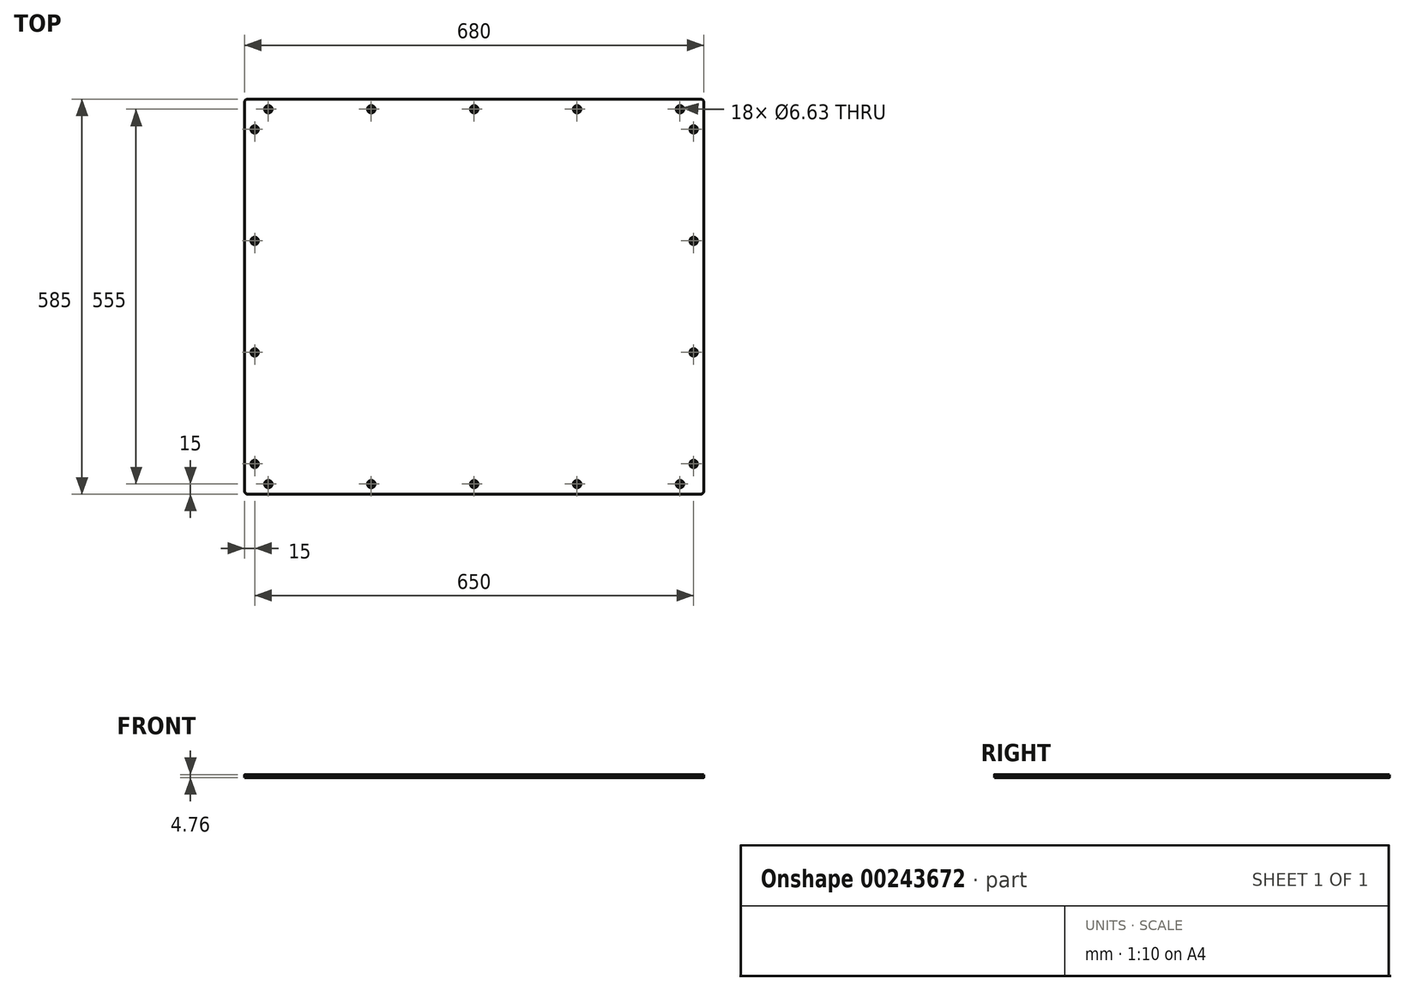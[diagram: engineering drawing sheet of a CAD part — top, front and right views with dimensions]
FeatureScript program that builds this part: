
annotation { "Feature Type Name" : "Feature", "Feature Type Description" : "" }
export const myFeature = defineFeature(function(context is Context, id is Id, definition is map)
    precondition{}
    {
        {
            var Q0;
            Q0=qCreatedBy(makeId("Top.planeOp"),FACE);
            var sketch = newSketch(context, id + "F0", { "sketchPlane" : qUnion([Q0])});
            skLineSegment(sketch, "E0.bottom", {"start": v(-340, -292.5) * mm, "end": v(340, -292.5) * mm});
            skLineSegment(sketch, "E0.top", {"start": v(-340, 292.5) * mm, "end": v(340, 292.5) * mm});
            skLineSegment(sketch, "E0.left", {"start": v(-340, -292.5) * mm, "end": v(-340, 292.5) * mm});
            skLineSegment(sketch, "E0.right", {"start": v(340, -292.5) * mm, "end": v(340, 292.5) * mm});
            skPoint(sketch, "E0.middle", {"position": v(0, 0) * mm});
            skSolve(sketch);
        }
        {
            var Q0;
            Q0 = qSketchRegion(id + "F0", true);
            extrude(context, id + "F1", {"entities" : qUnion([Q0]), "endBound" : BoundingType.SYMMETRIC, "depth" : 4.76 * mm});
        }
        {
            var Q0;
            Q0=makeQuery(id+"F1.opExtrude","SWEPT_EDGE",EDGE,{"disambiguationData":[OSD([sQuery(id+"F0.wireOp",EDGE,"E0.top"),sQuery(id+"F0.wireOp",EDGE,"E0.right")])]});
            var Q1;
            Q1=makeQuery(id+"F1.opExtrude","SWEPT_EDGE",EDGE,{"disambiguationData":[OSD([sQuery(id+"F0.wireOp",EDGE,"E0.bottom"),sQuery(id+"F0.wireOp",EDGE,"E0.right")])]});
            var Q2;
            Q2=makeQuery(id+"F1.opExtrude","SWEPT_EDGE",EDGE,{"disambiguationData":[OSD([sQuery(id+"F0.wireOp",EDGE,"E0.bottom"),sQuery(id+"F0.wireOp",EDGE,"E0.left")])]});
            var Q3;
            Q3=makeQuery(id+"F1.opExtrude","SWEPT_EDGE",EDGE,{"disambiguationData":[OSD([sQuery(id+"F0.wireOp",EDGE,"E0.top"),sQuery(id+"F0.wireOp",EDGE,"E0.left")])]});
            fillet(context, id + "F2", {"entities" : qUnion([Q0, Q1, Q2, Q3]), "radius" : 4.76 * mm, "tangentPropagation" : true, "allowEdgeOverflow" : false});
        }
        {
            var Q0;
            Q0=makeQuery(id+"F1.opExtrude","CAP_FACE",FACE,{"disambiguationData":[OSD([sQuery(id+"F0.wireOp",EDGE,"E0.bottom"),sQuery(id+"F0.wireOp",EDGE,"E0.top"),sQuery(id+"F0.wireOp",EDGE,"E0.left"),sQuery(id+"F0.wireOp",EDGE,"E0.right")])],"isStart":false});
            var sketch = newSketch(context, id + "F3", { "sketchPlane" : qUnion([Q0])});
            skLineSegment(sketch, "E1", {"start": v(-325, 247.65) * mm, "end": v(-325, 165.1) * mm, "construction": true});
            skLineSegment(sketch, "E2", {"start": v(-325, 165.1) * mm, "end": v(-325, 82.55) * mm, "construction": true});
            skLineSegment(sketch, "E3", {"start": v(-325, 82.55) * mm, "end": v(-325, 0) * mm, "construction": true});
            skLineSegment(sketch, "E4", {"start": v(-325, 0) * mm, "end": v(0, 0) * mm, "construction": true});
            skLineSegment(sketch, "E5", {"start": v(-325, 0) * mm, "end": v(-325, -82.55) * mm, "construction": true});
            skLineSegment(sketch, "E6", {"start": v(-325, -82.55) * mm, "end": v(-325, -165.1) * mm, "construction": true});
            skLineSegment(sketch, "E7", {"start": v(-325, -165.1) * mm, "end": v(-325, -247.65) * mm, "construction": true});
            skLineSegment(sketch, "E8", {"start": v(0, 0) * mm, "end": v(0, 277.5) * mm, "construction": true});
            skLineSegment(sketch, "E9", {"start": v(0, 277.5) * mm, "end": v(-76.2, 277.5) * mm, "construction": true});
            skLineSegment(sketch, "E10", {"start": v(-76.2, 277.5) * mm, "end": v(-152.4, 277.5) * mm, "construction": true});
            skLineSegment(sketch, "E11", {"start": v(-152.4, 277.5) * mm, "end": v(-228.6, 277.5) * mm, "construction": true});
            skLineSegment(sketch, "E12", {"start": v(-228.6, 277.5) * mm, "end": v(-304.8, 277.5) * mm, "construction": true});
            skLineSegment(sketch, "E13", {"start": v(0, 277.5) * mm, "end": v(76.2, 277.5) * mm, "construction": true});
            skLineSegment(sketch, "E14", {"start": v(76.2, 277.5) * mm, "end": v(152.4, 277.5) * mm, "construction": true});
            skLineSegment(sketch, "E15", {"start": v(152.4, 277.5) * mm, "end": v(228.6, 277.5) * mm, "construction": true});
            skLineSegment(sketch, "E16", {"start": v(228.6, 277.5) * mm, "end": v(304.8, 277.5) * mm, "construction": true});
            skLineSegment(sketch, "E17.MirrorCS", {"start": v(228.6, -277.5) * mm, "end": v(304.8, -277.5) * mm, "construction": true});
            skLineSegment(sketch, "E18.MirrorCS", {"start": v(152.4, -277.5) * mm, "end": v(228.6, -277.5) * mm, "construction": true});
            skLineSegment(sketch, "E19.MirrorCS", {"start": v(76.2, -277.5) * mm, "end": v(152.4, -277.5) * mm, "construction": true});
            skLineSegment(sketch, "E20.MirrorCS", {"start": v(0, -277.5) * mm, "end": v(76.2, -277.5) * mm, "construction": true});
            skLineSegment(sketch, "E21.MirrorCS", {"start": v(-228.6, -277.5) * mm, "end": v(-304.8, -277.5) * mm, "construction": true});
            skLineSegment(sketch, "E22.MirrorCS", {"start": v(-152.4, -277.5) * mm, "end": v(-228.6, -277.5) * mm, "construction": true});
            skLineSegment(sketch, "E23.MirrorCS", {"start": v(-76.2, -277.5) * mm, "end": v(-152.4, -277.5) * mm, "construction": true});
            skLineSegment(sketch, "E24.MirrorCS", {"start": v(0, -277.5) * mm, "end": v(-76.2, -277.5) * mm, "construction": true});
            skLineSegment(sketch, "E25.MirrorCS", {"start": v(325, 247.65) * mm, "end": v(325, 165.1) * mm, "construction": true});
            skLineSegment(sketch, "E26.MirrorCS", {"start": v(325, 165.1) * mm, "end": v(325, 82.55) * mm, "construction": true});
            skLineSegment(sketch, "E27.MirrorCS", {"start": v(325, 82.55) * mm, "end": v(325, 0) * mm, "construction": true});
            skLineSegment(sketch, "E28.MirrorCS", {"start": v(325, -82.55) * mm, "end": v(325, -165.1) * mm, "construction": true});
            skLineSegment(sketch, "E29.MirrorCS", {"start": v(325, 0) * mm, "end": v(325, -82.55) * mm, "construction": true});
            skLineSegment(sketch, "E30.MirrorCS", {"start": v(325, -165.1) * mm, "end": v(325, -247.65) * mm, "construction": true});
            skSolve(sketch);
        }
        {
            var Q0;
            Q0=sQuery(id+"F3.wireOp",VERTEX,"E3.start");
            var Q1;
            Q1=sQuery(id+"F3.wireOp",VERTEX,"E1.start");
            var Q2;
            Q2=sQuery(id+"F3.wireOp",VERTEX,"E6.start");
            var Q3;
            Q3=sQuery(id+"F3.wireOp",VERTEX,"E7.end");
            var Q4;
            Q4=sQuery(id+"F3.wireOp",VERTEX,"E21.MirrorCS.end");
            var Q5;
            Q5=sQuery(id+"F3.wireOp",VERTEX,"E23.MirrorCS.end");
            var Q6;
            Q6=sQuery(id+"F3.wireOp",VERTEX,"E20.MirrorCS.start");
            var Q7;
            Q7=sQuery(id+"F3.wireOp",VERTEX,"E18.MirrorCS.start");
            var Q8;
            Q8=sQuery(id+"F3.wireOp",VERTEX,"E17.MirrorCS.end");
            var Q9;
            Q9=sQuery(id+"F3.wireOp",VERTEX,"E30.MirrorCS.end");
            var Q10;
            Q10=sQuery(id+"F3.wireOp",VERTEX,"E29.MirrorCS.end");
            var Q11;
            Q11=sQuery(id+"F3.wireOp",VERTEX,"E27.MirrorCS.start");
            var Q12;
            Q12=sQuery(id+"F3.wireOp",VERTEX,"E25.MirrorCS.start");
            var Q13;
            Q13=sQuery(id+"F3.wireOp",VERTEX,"E16.end");
            var Q14;
            Q14=sQuery(id+"F3.wireOp",VERTEX,"E14.end");
            var Q15;
            Q15=sQuery(id+"F3.wireOp",VERTEX,"E8.end");
            var Q16;
            Q16=sQuery(id+"F3.wireOp",VERTEX,"E11.start");
            var Q17;
            Q17=sQuery(id+"F3.wireOp",VERTEX,"E12.end");
            var Q18;
            Q18=makeQuery(id+"F1.opExtrude","SWEPT_BODY",BODY,{"disambiguationData":[OSD([sQuery(id+"F0.wireOp",EDGE,"E0.bottom"),sQuery(id+"F0.wireOp",EDGE,"E0.top"),sQuery(id+"F0.wireOp",EDGE,"E0.left"),sQuery(id+"F0.wireOp",EDGE,"E0.right")])]});
            hole(context, id + "F4", {"style" : HoleStyle.C_SINK, "endStyle" : HoleEndStyle.THROUGH, "holeDiameter" : 6.63 * mm, "cSinkDiameter" : 11.2 * mm, "cSinkAngle" : 90 * degree, "tappedDepth" : 12.7 * mm, "tapClearance" : 3, "locations" : qUnion([Q0, Q1, Q2, Q3, Q4, Q5, Q6, Q7, Q8, Q9, Q10, Q11, Q12, Q13, Q14, Q15, Q16, Q17]), "scope" : qUnion([Q18])});
        }
    });
